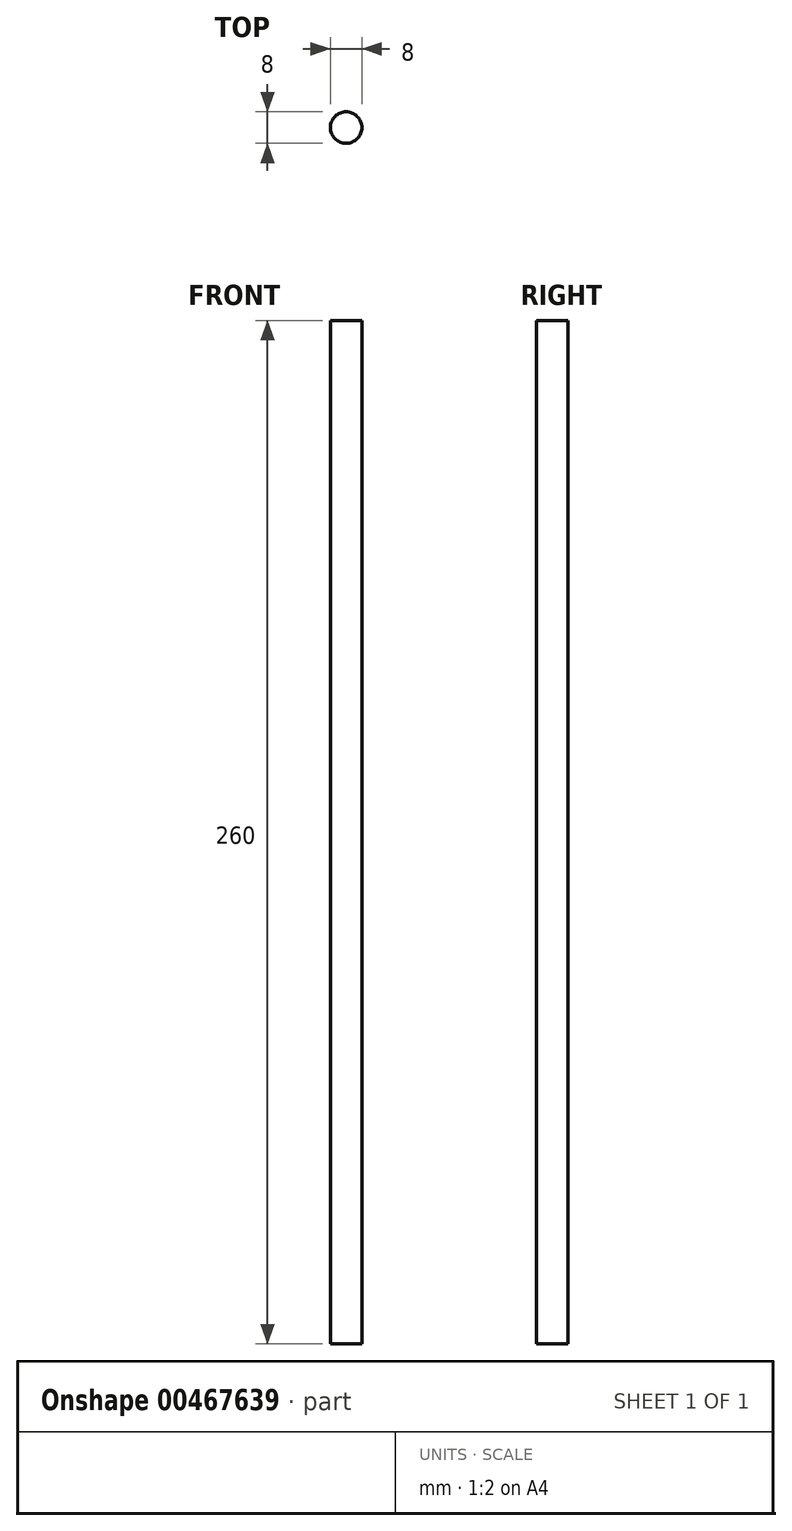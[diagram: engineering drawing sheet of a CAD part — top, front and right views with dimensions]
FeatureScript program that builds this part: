
annotation { "Feature Type Name" : "Feature", "Feature Type Description" : "" }
export const myFeature = defineFeature(function(context is Context, id is Id, definition is map)
    precondition{}
    {
        {
            var Q0;
            Q0=qCreatedBy(makeId("Top.planeOp"),FACE);
            var sketch = newSketch(context, id + "F0", { "sketchPlane" : qUnion([Q0])});
            skCircle(sketch, "E0", {"center": v(0, 0) * mm, "radius": 4 * mm});
            skSolve(sketch);
        }
        {
            var Q0;
            Q0 = qSketchRegion(id + "F0", true);
            extrude(context, id + "F1", {"entities" : qUnion([Q0]), "depth" : 260 * mm});
        }
    });
